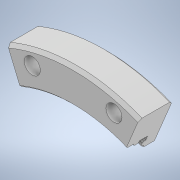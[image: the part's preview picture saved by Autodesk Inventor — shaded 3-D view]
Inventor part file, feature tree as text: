
AUTODESK INVENTOR PART (.ipt)
format: ipt  version: 2021 (Build 250183000, 183)  size: 164,352 bytes
history: native  units: mm
features: chamfer x2, sketch x2, revolve x1, extrude x1
ambient origin geometry x8: Origin, YZ Plane, XZ Plane, XY Plane, X Axis, Y Axis, Z Axis, Center Point
bodies: Solid1 (feature_tree)
feature tree (6):
  revolve  "Revolution1"  [1 undecoded]
  chamfer  "Chamfer2"  Distance=2.0mm
  chamfer  "Chamfer3"  Distance=5.0mm
  extrude  "Extrusion4"  Depth=2.0mm
  sketch  "Sketch1"  dims[d0=4.0mm d1=9.0mm]
  sketch  "Sketch5"  dims[d2=3.0mm d3=2.0mm d4=5.0mm d5=4.0mm d6=90.2mm d7=45.0deg d8=20.0mm d9=2.0mm d13=1.0mm d14=2.0mm d15=45.0deg d21=81.2mm d22=8.0mm d23=14.0mm d25=22.0mm d37=2.0mm d38=2.0mm d39=45.0deg d40=0.0mm d41=103.0mm d42=10.5mm d43=15.0deg d44=0.0mm d45=0.0mm]
note: 1 required parameter value undecoded (feature->parameter linkage not recoverable at this tier; creation-order binding heuristic only, values carry confidence <= 0.55)
